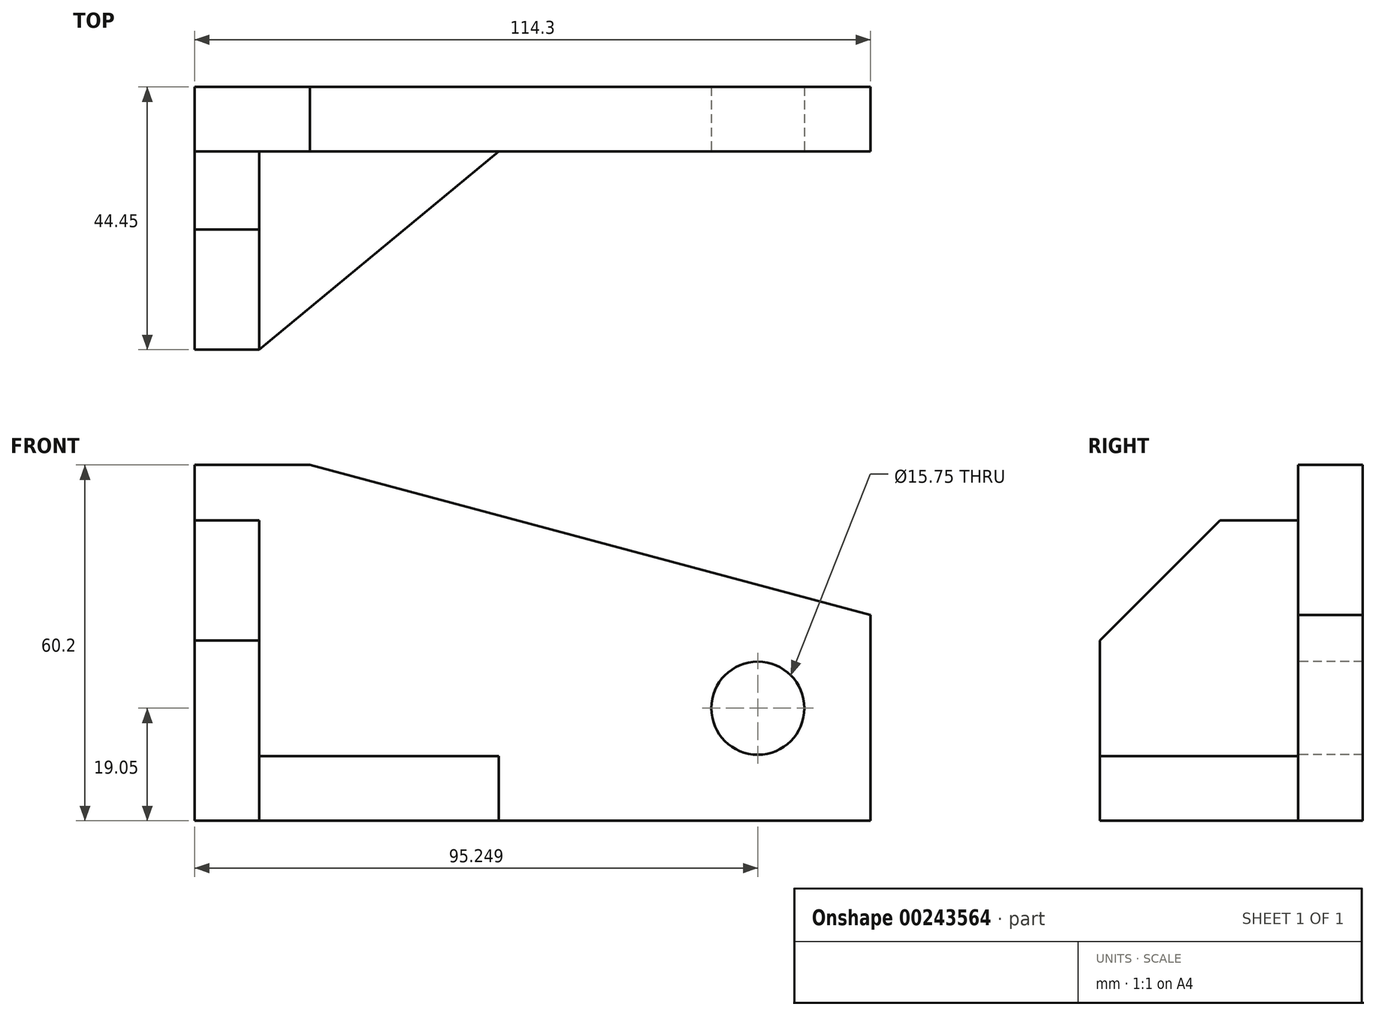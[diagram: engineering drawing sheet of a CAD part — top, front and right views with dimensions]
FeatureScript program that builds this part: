
annotation { "Feature Type Name" : "Feature", "Feature Type Description" : "" }
export const myFeature = defineFeature(function(context is Context, id is Id, definition is map)
    precondition{}
    {
        {
            var Q0;
            Q0=qCreatedBy(makeId("Top.planeOp"),FACE);
            var sketch = newSketch(context, id + "F0", { "sketchPlane" : qUnion([Q0])});
            skLineSegment(sketch, "E0.bottom", {"start": v(-73.55, 21.84) * mm, "end": v(40.75, 21.84) * mm});
            skLineSegment(sketch, "E0.right", {"start": v(40.75, 21.84) * mm, "end": v(40.75, 10.92) * mm});
            skLineSegment(sketch, "E1", {"start": v(-22.13, 10.92) * mm, "end": v(40.75, 10.92) * mm});
            skLineSegment(sketch, "E2", {"start": v(-73.55, -22.6) * mm, "end": v(-62.63, -22.6) * mm});
            skLineSegment(sketch, "E3", {"start": v(-62.63, -22.6) * mm, "end": v(-22.13, 10.92) * mm});
            skLineSegment(sketch, "E4", {"start": v(-73.55, 21.84) * mm, "end": v(-73.55, -22.6) * mm});
            skLineSegment(sketch, "E5", {"start": v(-22.13, 10.92) * mm, "end": v(-73.55, 10.92) * mm});
            skSolve(sketch);
        }
        {
            var Q0;
            {var subQ0=sQuery(id+"F0.wireOp",EDGE,"E2");Q0=makeQuery(id+"F0.imprint","IMPRINT",FACE,{"disambiguationData":[TD([[makeQuery(id+"F0.imprint","IMPRINT",EDGE,{"derivedFrom":subQ0}),1.0]])]});}
            var Q1;
            {var subQ1=sQuery(id+"F0.wireOp",EDGE,"E0.bottom");Q1=makeQuery(id+"F0.imprint","IMPRINT",FACE,{"disambiguationData":[TD([[makeQuery(id+"F0.imprint","IMPRINT",EDGE,{"derivedFrom":subQ1}),-1.0]])]});}
            extrude(context, id + "F1", {"entities" : qUnion([Q0, Q1]), "depth" : 10.92 * mm});
        }
        {
            var Q0;
            {var subQ1=sQuery(id+"F0.wireOp",EDGE,"E0.bottom");Q0=makeQuery(id+"F0.imprint","IMPRINT",FACE,{"disambiguationData":[TD([[makeQuery(id+"F0.imprint","IMPRINT",EDGE,{"derivedFrom":subQ1}),-1.0]])]});}
            extrude(context, id + "F2", {"entities" : qUnion([Q0]), "operationType" : NewBodyOperationType.ADD, "depth" : 60.2 * mm});
        }
        {
            var Q0;
            {var subQ0=sQuery(id+"F0.wireOp",EDGE,"E1");Q0=makeQuery(id+"F2.boolean.opBoolean","MERGE",FACE,{"derivedFrom":[makeQuery(id+"F1.opExtrude","SWEPT_FACE",FACE,{"disambiguationData":[OSD([subQ0])]}),makeQuery(id+"F2.opExtrude","SWEPT_FACE",FACE,{"disambiguationData":[OSD([subQ0,sQuery(id+"F0.wireOp",EDGE,"E5")])]})]});}
            var sketch = newSketch(context, id + "F3", { "sketchPlane" : qUnion([Q0])});
            skLineSegment(sketch, "E6", {"start": v(-73.55, 60.2) * mm, "end": v(-41.8, 60.2) * mm});
            skLineSegment(sketch, "E7", {"start": v(-73.55, 10.92) * mm, "end": v(-73.55, 50.8) * mm});
            skCircle(sketch, "E8", {"center": v(21.7, 19.05) * mm, "radius": 7.87 * mm});
            skSolve(sketch);
        }
        {
            var Q0;
            Q0=makeQuery(id+"F1.opExtrude","CAP_FACE",FACE,{"disambiguationData":[OSD([sQuery(id+"F0.wireOp",EDGE,"E0.bottom"),sQuery(id+"F0.wireOp",EDGE,"E0.right"),sQuery(id+"F0.wireOp",EDGE,"E1"),sQuery(id+"F0.wireOp",EDGE,"E2"),sQuery(id+"F0.wireOp",EDGE,"E3"),sQuery(id+"F0.wireOp",EDGE,"E4")])],"isStart":false});
            var sketch = newSketch(context, id + "F4", { "sketchPlane" : qUnion([Q0])});
            skLineSegment(sketch, "E9", {"start": v(-62.63, -22.6) * mm, "end": v(-62.63, 10.92) * mm});
            skLineSegment(sketch, "E10", {"start": v(-62.63, 10.92) * mm, "end": v(-73.55, 10.92) * mm});
            skSolve(sketch);
        }
        {
            var Q0;
            Q0=makeQuery(id+"F4.imprint","IMPRINT",FACE,{"disambiguationData":[TD([[makeQuery(id+"F4.imprint","IMPRINT",EDGE,{"derivedFrom":sQuery(id+"F4.wireOp",EDGE,"E9")}),1.0]])]});
            extrude(context, id + "F5", {"entities" : qUnion([Q0]), "operationType" : NewBodyOperationType.ADD, "depth" : 39.88 * mm});
        }
        {
            var Q0;
            Q0=makeQuery(id+"F5.opExtrude","CAP_EDGE",EDGE,{"disambiguationData":[OSD([sQuery(id+"F0.wireOp",EDGE,"E2")])],"isStart":false});
            chamfer(context, id + "F6", {"entities" : qUnion([Q0]), "width" : 20.32 * mm, "tangentPropagation" : true});
        }
        {
            var Q0;
            Q0=makeQuery(id+"F2.opExtrude","CAP_EDGE",EDGE,{"disambiguationData":[OSD([sQuery(id+"F0.wireOp",EDGE,"E0.right")])],"isStart":false});
            chamfer(context, id + "F7", {"entities" : qUnion([Q0]), "chamferType" : ChamferType.OFFSET_ANGLE, "width" : 25.4 * mm, "oppositeDirection" : false, "angle" : 75 * degree, "tangentPropagation" : true});
        }
        {
            var Q0;
            Q0=sQuery(id+"F3.wireOp",VERTEX,"E8.center");
            var Q1;
            Q1=makeQuery(id+"F1.opExtrude","SWEPT_BODY",BODY,{"disambiguationData":[OSD([sQuery(id+"F0.wireOp",EDGE,"E0.bottom"),sQuery(id+"F0.wireOp",EDGE,"E0.right"),sQuery(id+"F0.wireOp",EDGE,"E1"),sQuery(id+"F0.wireOp",EDGE,"E2"),sQuery(id+"F0.wireOp",EDGE,"E3"),sQuery(id+"F0.wireOp",EDGE,"E4")])]});
            hole(context, id + "F8", {"style" : HoleStyle.SIMPLE, "endStyle" : HoleEndStyle.BLIND, "holeDiameter" : 15.75 * mm, "holeDepth" : 10.92 * mm, "tappedDepth" : 12.7 * mm, "tapClearance" : 3, "startFromSketch" : true, "locations" : qUnion([Q0]), "scope" : qUnion([Q1])});
        }
    });
